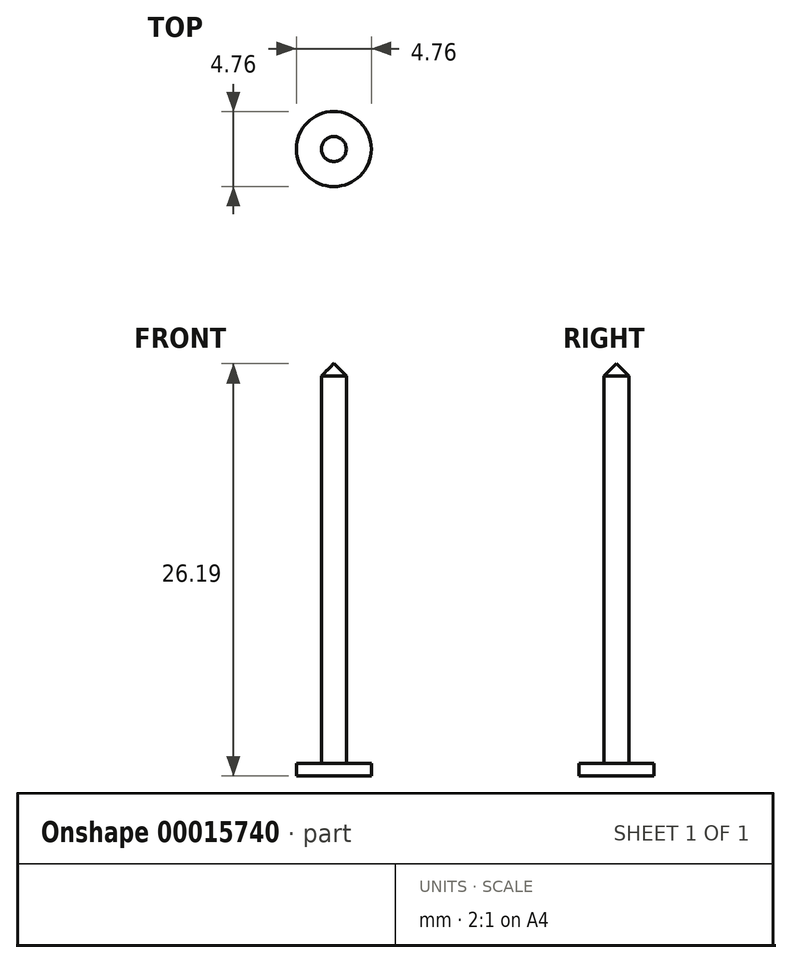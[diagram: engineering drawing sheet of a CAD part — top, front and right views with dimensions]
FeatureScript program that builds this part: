
annotation { "Feature Type Name" : "Feature", "Feature Type Description" : "" }
export const myFeature = defineFeature(function(context is Context, id is Id, definition is map)
    precondition{}
    {
        {
            var Q0;
            Q0=qCreatedBy(makeId("Top.planeOp"),FACE);
            var sketch = newSketch(context, id + "F0", { "sketchPlane" : qUnion([Q0])});
            skCircle(sketch, "E0", {"center": v(0, 0) * mm, "radius": 2.38 * mm});
            skSolve(sketch);
        }
        {
            var Q0;
            Q0 = qSketchRegion(id + "F0", true);
            extrude(context, id + "F1", {"entities" : qUnion([Q0]), "depth" : 0.8 * mm});
        }
        {
            var Q0;
            Q0=makeQuery(id+"F1.opExtrude","CAP_FACE",FACE,{"disambiguationData":[OSD([sQuery(id+"F0.wireOp",EDGE,"E0")])],"isStart":false});
            var sketch = newSketch(context, id + "F2", { "sketchPlane" : qUnion([Q0])});
            skCircle(sketch, "E1", {"center": v(0, 0) * mm, "radius": 0.8 * mm});
            skSolve(sketch);
        }
        {
            var Q0;
            Q0 = qSketchRegion(id + "F2", true);
            extrude(context, id + "F3", {"entities" : qUnion([Q0]), "operationType" : NewBodyOperationType.ADD, "depth" : 25.4 * mm});
        }
        {
            var Q0;
            Q0=makeQuery(id+"F3.opExtrude","CAP_EDGE",EDGE,{"disambiguationData":[OSD([sQuery(id+"F2.wireOp",EDGE,"E1")])],"isStart":false});
            chamfer(context, id + "F4", {"entities" : qUnion([Q0]), "width" : 0.8 * mm, "tangentPropagation" : true});
        }
    });
